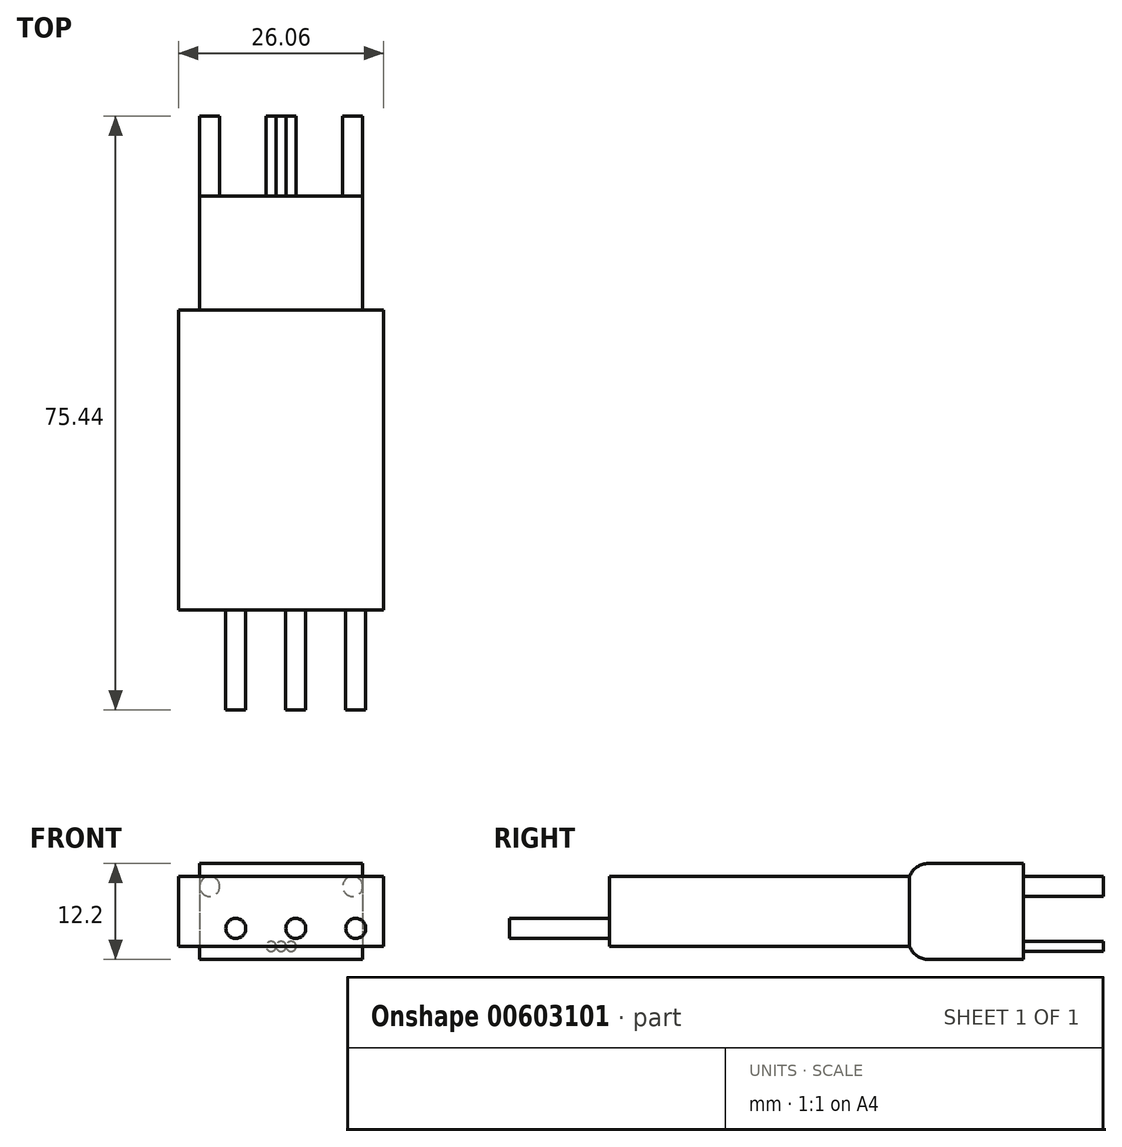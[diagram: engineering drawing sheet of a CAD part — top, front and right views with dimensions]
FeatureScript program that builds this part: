
annotation { "Feature Type Name" : "Feature", "Feature Type Description" : "" }
export const myFeature = defineFeature(function(context is Context, id is Id, definition is map)
    precondition{}
    {
        {
            var Q0;
            Q0=qCreatedBy(makeId("Top.planeOp"),FACE);
            var sketch = newSketch(context, id + "F0", { "sketchPlane" : qUnion([Q0])});
            skLineSegment(sketch, "E0.bottom", {"start": v(13.03, 19.05) * mm, "end": v(-13.03, 19.05) * mm});
            skLineSegment(sketch, "E0.top", {"start": v(13.03, -19.05) * mm, "end": v(-13.03, -19.05) * mm});
            skLineSegment(sketch, "E0.left", {"start": v(13.03, 19.05) * mm, "end": v(13.03, -19.05) * mm});
            skLineSegment(sketch, "E0.right", {"start": v(-13.03, 19.05) * mm, "end": v(-13.03, -19.05) * mm});
            skPoint(sketch, "E0.middle", {"position": v(0, 0) * mm});
            skSolve(sketch);
        }
        {
            var Q0;
            Q0 = qSketchRegion(id + "F0", true);
            extrude(context, id + "F1", {"entities" : qUnion([Q0]), "endBound" : BoundingType.SYMMETRIC, "depth" : 8.9 * mm, "offsetDistance" : 25.4 * mm});
        }
        {
            var Q0;
            Q0=makeQuery(id+"F1.opExtrude","SWEPT_FACE",FACE,{"disambiguationData":[OSD([sQuery(id+"F0.wireOp",EDGE,"E0.top")])]});
            var sketch = newSketch(context, id + "F2", { "sketchPlane" : qUnion([Q0])});
            skCircle(sketch, "E1", {"center": v(-5.77, -2.16) * mm, "radius": 1.27 * mm});
            skCircle(sketch, "E2", {"center": v(1.85, -2.16) * mm, "radius": 1.27 * mm});
            skCircle(sketch, "E3", {"center": v(9.47, -2.16) * mm, "radius": 1.27 * mm});
            skSolve(sketch);
        }
        {
            var Q0;
            Q0 = qSketchRegion(id + "F2", true);
            extrude(context, id + "F3", {"entities" : qUnion([Q0]), "operationType" : NewBodyOperationType.ADD, "depth" : 12.7 * mm, "offsetDistance" : 25.4 * mm});
        }
        {
            var Q0;
            Q0=makeQuery(id+"F1.opExtrude","SWEPT_FACE",FACE,{"disambiguationData":[OSD([sQuery(id+"F0.wireOp",EDGE,"E0.bottom")])]});
            var sketch = newSketch(context, id + "F4", { "sketchPlane" : qUnion([Q0])});
            skLineSegment(sketch, "E4.bottom", {"start": v(10.35, 6.1) * mm, "end": v(-10.35, 6.1) * mm});
            skLineSegment(sketch, "E4.top", {"start": v(10.35, -6.1) * mm, "end": v(-10.35, -6.1) * mm});
            skLineSegment(sketch, "E4.left", {"start": v(10.35, 6.1) * mm, "end": v(10.35, -6.1) * mm});
            skLineSegment(sketch, "E4.right", {"start": v(-10.35, 6.1) * mm, "end": v(-10.35, -6.1) * mm});
            skPoint(sketch, "E4.middle", {"position": v(0, 0) * mm});
            skSolve(sketch);
        }
        {
            var Q0;
            Q0 = qSketchRegion(id + "F4", true);
            extrude(context, id + "F5", {"entities" : qUnion([Q0]), "operationType" : NewBodyOperationType.ADD, "depth" : 14.48 * mm, "offsetDistance" : 25.4 * mm});
        }
        {
            var Q0;
            Q0=makeQuery(id+"F5.opExtrude","CAP_FACE",FACE,{"disambiguationData":[OSD([sQuery(id+"F4.wireOp",EDGE,"E4.bottom"),sQuery(id+"F4.wireOp",EDGE,"E4.top"),sQuery(id+"F4.wireOp",EDGE,"E4.left"),sQuery(id+"F4.wireOp",EDGE,"E4.right")])],"isStart":false});
            var sketch = newSketch(context, id + "F6", { "sketchPlane" : qUnion([Q0])});
            skCircle(sketch, "E5", {"center": v(-9.08, 3.17) * mm, "radius": 1.27 * mm});
            skCircle(sketch, "E6", {"center": v(9.08, 3.17) * mm, "radius": 1.27 * mm});
            skCircle(sketch, "E7", {"center": v(0, -4.45) * mm, "radius": 0.64 * mm});
            skCircle(sketch, "E8", {"center": v(1.27, -4.45) * mm, "radius": 0.64 * mm});
            skCircle(sketch, "E9", {"center": v(-1.27, -4.45) * mm, "radius": 0.64 * mm});
            skSolve(sketch);
        }
        {
            var Q0;
            Q0 = qSketchRegion(id + "F6", true);
            extrude(context, id + "F7", {"entities" : qUnion([Q0]), "depth" : 10.16 * mm, "offsetDistance" : 25.4 * mm});
        }
        {
            var Q0;
            Q0=makeQuery(id+"F5.opExtrude","CAP_EDGE",EDGE,{"disambiguationData":[OSD([sQuery(id+"F4.wireOp",EDGE,"E4.bottom")])],"isStart":true});
            var Q1;
            Q1=makeQuery(id+"F5.opExtrude","CAP_EDGE",EDGE,{"disambiguationData":[OSD([sQuery(id+"F4.wireOp",EDGE,"E4.top")])],"isStart":true});
            fillet(context, id + "F8", {"entities" : qUnion([Q0, Q1]), "radius" : 2.54 * mm, "tangentPropagation" : true, "allowEdgeOverflow" : false});
        }
    });
